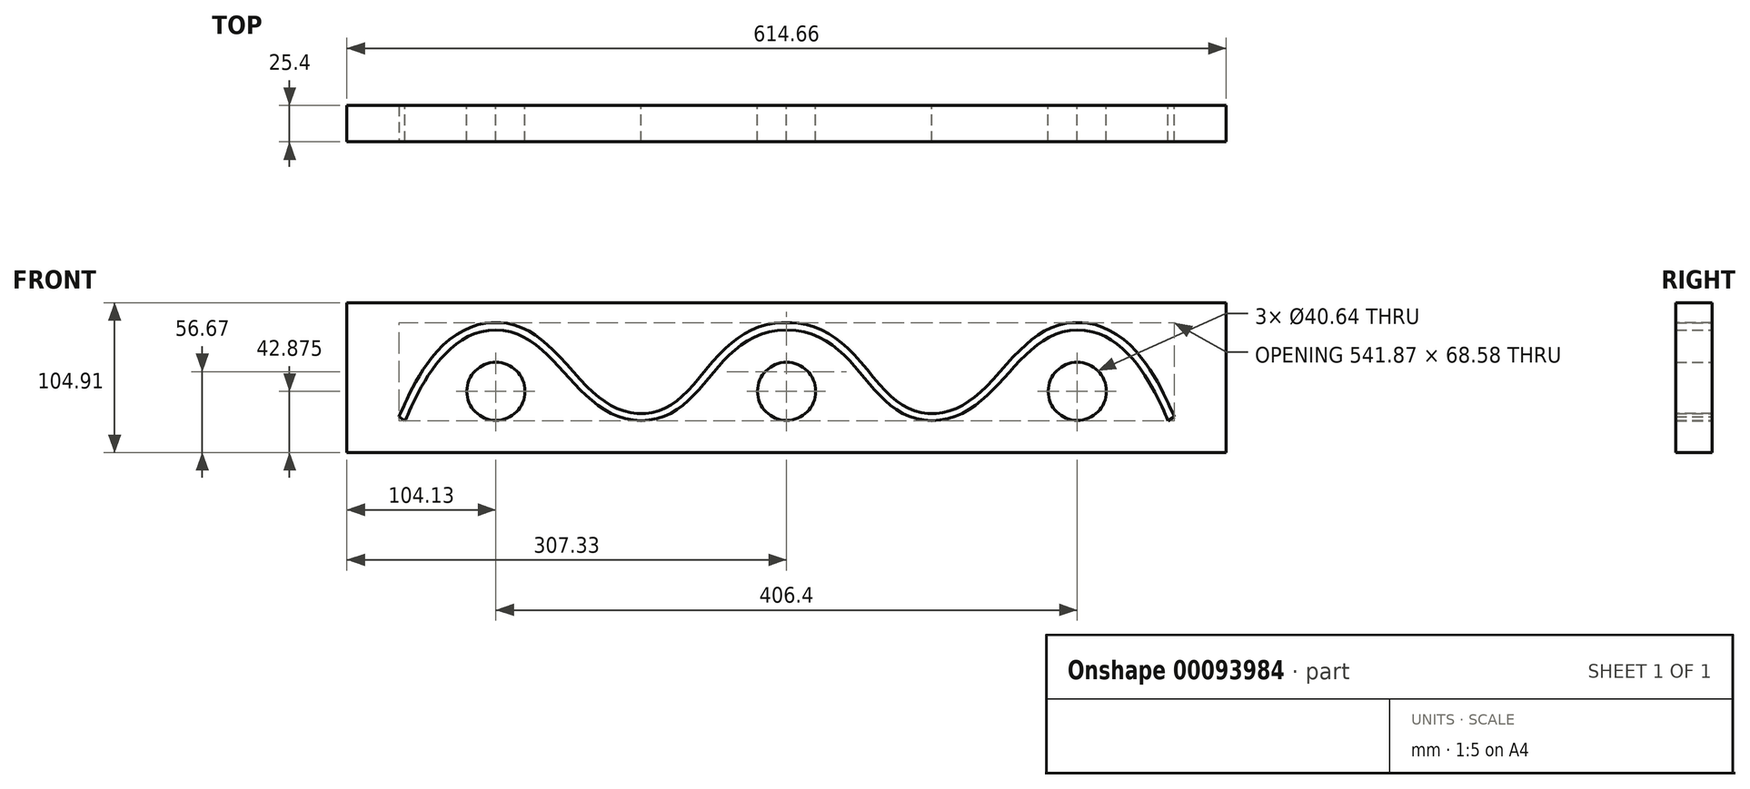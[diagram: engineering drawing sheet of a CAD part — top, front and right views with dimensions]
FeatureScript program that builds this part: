
annotation { "Feature Type Name" : "Feature", "Feature Type Description" : "" }
export const myFeature = defineFeature(function(context is Context, id is Id, definition is map)
    precondition{}
    {
        {
            var Q0;
            Q0=qCreatedBy(makeId("Front.planeOp"),FACE);
            var sketch = newSketch(context, id + "F0", { "sketchPlane" : qUnion([Q0])});
            skFitSpline(sketch, "E0", {"points": [v(0, 63.5) * mm, v(-101.6, 0) * mm], "startDerivative": vector(-152.4, 0) * mm, "endDerivative": vector(-136.45, 0) * mm});
            skFitSpline(sketch, "E1", {"points": [v(-101.6, 0) * mm, v(-203.2, 63.5) * mm], "startDerivative": vector(-136.45, 0) * mm, "endDerivative": vector(-125.77, 0) * mm});
            skFitSpline(sketch, "E2", {"points": [v(-203.2, 63.5) * mm, v(-266.7, 0) * mm], "startDerivative": vector(-123.42, 0) * mm, "endDerivative": vector(-9.52, -14.37) * mm});
            skFitSpline(sketch, "E3.MirrorCS", {"points": [v(0, 63.5) * mm, v(101.6, 0) * mm], "startDerivative": vector(152.4, 0) * mm, "endDerivative": vector(136.45, 0) * mm});
            skFitSpline(sketch, "E4.MirrorCS", {"points": [v(101.6, 0) * mm, v(203.2, 63.5) * mm], "startDerivative": vector(136.45, 0) * mm, "endDerivative": vector(125.77, 0) * mm});
            skFitSpline(sketch, "E5.MirrorCS", {"points": [v(203.2, 63.5) * mm, v(266.7, 0) * mm], "startDerivative": vector(123.42, 0) * mm, "endDerivative": vector(9.52, -14.37) * mm});
            skFitSpline(sketch, "E6.0", {"points": [v(-203.2, 68.58) * mm, v(-206.07, 68.58) * mm, v(-211.66, 68.07) * mm, v(-219.45, 65.93) * mm, v(-226.61, 62.66) * mm, v(-235.32, 57.06) * mm, v(-242.8, 50.05) * mm, v(-249.2, 42.33) * mm, v(-253.5, 36.37) * mm, v(-257.29, 30.38) * mm, v(-260.61, 24.54) * mm, v(-263.48, 19.01) * mm, v(-265.5, 14.8) * mm, v(-266.91, 11.75) * mm, v(-267.86, 9.64) * mm, v(-268.7, 7.75) * mm, v(-269.43, 6.08) * mm, v(-269.94, 4.91) * mm, v(-270.3, 4.13) * mm, v(-270.53, 3.63) * mm, v(-270.7, 3.28) * mm, v(-270.8, 3.07) * mm, v(-270.87, 2.93) * mm, v(-270.92, 2.85) * mm, v(-270.94, 2.8) * mm, v(-270.95, 2.78) * mm, v(-270.96, 2.77) * mm, v(-270.96, 2.76) * mm, v(-270.96, 2.76) * mm, v(-270.96, 2.76) * mm, v(-270.96, 2.76) * mm, v(-270.96, 2.76) * mm, v(-270.97, 2.75) * mm, v(-270.98, 2.74) * mm, v(-270.99, 2.72) * mm, v(-271, 2.7) * mm, v(-271.03, 2.65) * mm, v(-271.05, 2.61) * mm, v(-271.07, 2.6) * mm]});
            skFitSpline(sketch, "E6.1", {"points": [v(-101.6, 5.08) * mm, v(-104.15, 5.08) * mm, v(-108.98, 5.52) * mm, v(-115.65, 7.34) * mm, v(-121.9, 10.18) * mm, v(-127.86, 13.93) * mm, v(-133.59, 18.47) * mm, v(-141, 25.36) * mm, v(-149.96, 35.11) * mm, v(-159.04, 45.16) * mm, v(-166.77, 52.63) * mm, v(-172.9, 57.76) * mm, v(-179.52, 62.2) * mm, v(-186.72, 65.7) * mm, v(-194.58, 68.02) * mm, v(-200.26, 68.58) * mm, v(-203.2, 68.58) * mm]});
            skFitSpline(sketch, "E6.2", {"points": [v(203.2, 68.58) * mm, v(206.07, 68.58) * mm, v(211.66, 68.07) * mm, v(219.45, 65.93) * mm, v(226.61, 62.66) * mm, v(235.32, 57.06) * mm, v(242.8, 50.05) * mm, v(249.2, 42.33) * mm, v(253.5, 36.37) * mm, v(257.29, 30.38) * mm, v(260.61, 24.54) * mm, v(263.48, 19.01) * mm, v(265.5, 14.8) * mm, v(266.91, 11.75) * mm, v(267.86, 9.64) * mm, v(268.7, 7.75) * mm, v(269.43, 6.08) * mm, v(269.94, 4.91) * mm, v(270.3, 4.13) * mm, v(270.53, 3.63) * mm, v(270.7, 3.28) * mm, v(270.8, 3.07) * mm, v(270.87, 2.93) * mm, v(270.92, 2.85) * mm, v(270.94, 2.8) * mm, v(270.95, 2.78) * mm, v(270.96, 2.77) * mm, v(270.96, 2.76) * mm, v(270.96, 2.76) * mm, v(270.96, 2.76) * mm, v(270.96, 2.76) * mm, v(270.96, 2.76) * mm, v(270.97, 2.75) * mm, v(270.98, 2.74) * mm, v(270.99, 2.72) * mm, v(271, 2.7) * mm, v(271.03, 2.65) * mm, v(271.05, 2.61) * mm, v(271.07, 2.6) * mm]});
            skFitSpline(sketch, "E6.3", {"points": [v(101.6, 5.08) * mm, v(104.15, 5.08) * mm, v(108.98, 5.52) * mm, v(115.65, 7.34) * mm, v(121.9, 10.18) * mm, v(127.86, 13.93) * mm, v(133.59, 18.47) * mm, v(141, 25.36) * mm, v(149.96, 35.11) * mm, v(159.04, 45.16) * mm, v(166.77, 52.63) * mm, v(172.9, 57.76) * mm, v(179.52, 62.2) * mm, v(186.72, 65.7) * mm, v(194.58, 68.02) * mm, v(200.26, 68.58) * mm, v(203.2, 68.58) * mm]});
            skFitSpline(sketch, "E6.4", {"points": [v(0, 68.58) * mm, v(3.44, 68.58) * mm, v(10, 68.04) * mm, v(18.88, 65.79) * mm, v(26.85, 62.3) * mm, v(33.98, 57.83) * mm, v(40.38, 52.65) * mm, v(48.15, 45.1) * mm, v(56.78, 34.95) * mm, v(64.92, 25.17) * mm, v(71.58, 18.3) * mm, v(76.75, 13.8) * mm, v(82.17, 10.1) * mm, v(87.96, 7.31) * mm, v(94.3, 5.52) * mm, v(99.05, 5.08) * mm, v(101.6, 5.08) * mm]});
            skFitSpline(sketch, "E6.5", {"points": [v(0, 68.58) * mm, v(-3.44, 68.58) * mm, v(-10, 68.04) * mm, v(-18.88, 65.79) * mm, v(-26.85, 62.3) * mm, v(-33.98, 57.83) * mm, v(-40.38, 52.65) * mm, v(-48.15, 45.1) * mm, v(-56.78, 34.95) * mm, v(-64.92, 25.17) * mm, v(-71.58, 18.3) * mm, v(-76.75, 13.8) * mm, v(-82.17, 10.1) * mm, v(-87.96, 7.31) * mm, v(-94.3, 5.52) * mm, v(-99.05, 5.08) * mm, v(-101.6, 5.08) * mm]});
            skLineSegment(sketch, "E7", {"start": v(-270.94, 2.8) * mm, "end": v(-266.7, 0) * mm});
            skLineSegment(sketch, "E8", {"start": v(266.7, 0) * mm, "end": v(270.94, 2.8) * mm});
            skLineSegment(sketch, "E9.bottom", {"start": v(307.33, -22.38) * mm, "end": v(-307.33, -22.38) * mm});
            skLineSegment(sketch, "E9.top", {"start": v(307.33, 82.53) * mm, "end": v(-307.33, 82.53) * mm});
            skLineSegment(sketch, "E9.left", {"start": v(307.33, -22.38) * mm, "end": v(307.33, 82.53) * mm});
            skLineSegment(sketch, "E9.right", {"start": v(-307.33, -22.38) * mm, "end": v(-307.33, 82.53) * mm});
            skPoint(sketch, "E9.middle", {"position": v(0, 30.07) * mm});
            skCircle(sketch, "E10", {"center": v(0, 20.5) * mm, "radius": 20.32 * mm});
            skCircle(sketch, "E11", {"center": v(-203.2, 20.5) * mm, "radius": 20.32 * mm});
            skCircle(sketch, "E12", {"center": v(203.2, 20.5) * mm, "radius": 20.32 * mm});
            skSolve(sketch);
        }
        {
            var Q0;
            Q0 = qSketchRegion(id + "F0", true);
            extrude(context, id + "F1", {"entities" : qUnion([Q0]), "depth" : 25.4 * mm});
        }
    });
